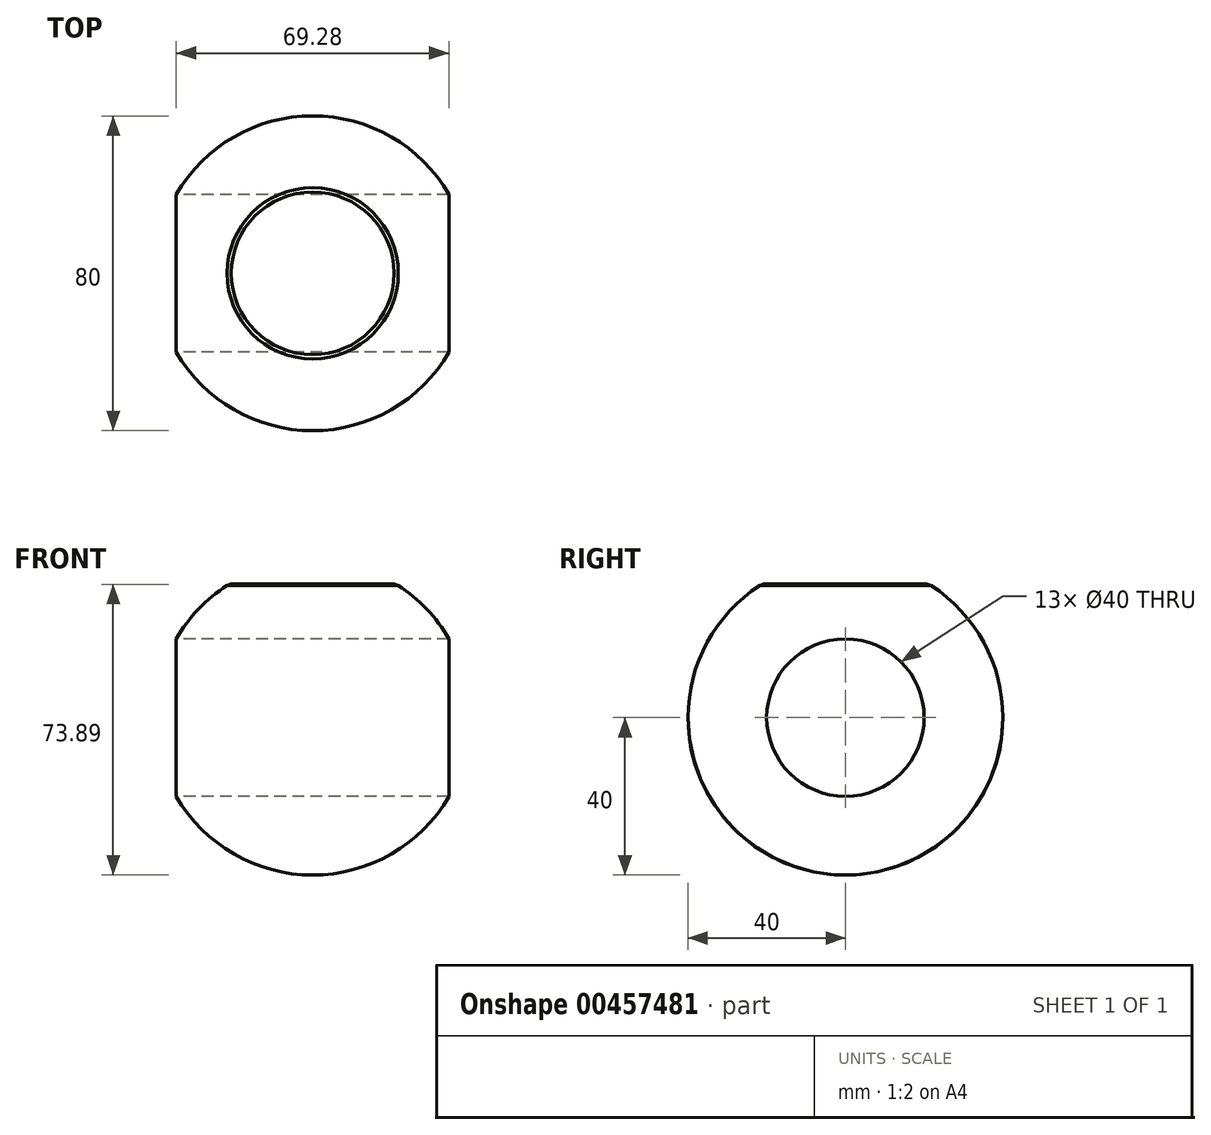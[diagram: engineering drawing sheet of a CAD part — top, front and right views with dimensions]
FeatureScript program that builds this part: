
annotation { "Feature Type Name" : "Feature", "Feature Type Description" : "" }
export const myFeature = defineFeature(function(context is Context, id is Id, definition is map)
    precondition{}
    {
        {
            var Q0;
            Q0=qCreatedBy(makeId("Top.planeOp"),FACE);
            var sketch = newSketch(context, id + "F0", { "sketchPlane" : qUnion([Q0])});
            skArc(sketch, "E0", {"start": v(0, -40) * mm, "mid": v(40, 0) * mm, "end": v(0, 40) * mm});
            skLineSegment(sketch, "E1", {"start": v(0, 40) * mm, "end": v(0, -40) * mm});
            skSolve(sketch);
        }
        {
            var Q0;
            Q0=makeQuery(id+"F0.imprint","IMPRINT",FACE,{"disambiguationData":[TD([[makeQuery(id+"F0.imprint","IMPRINT",EDGE,{"derivedFrom":sQuery(id+"F0.wireOp",EDGE,"E0")}),1.0]])]});
            var Q1;
            Q1=sQuery(id+"F0.wireOp",EDGE,"E1");
            revolve(context, id + "F1", {"entities" : qUnion([Q0]), "axis" : qUnion([Q1]), "revolveType" : RevolveType.FULL});
        }
        {
            var Q0;
            Q0=qCreatedBy(makeId("Right.planeOp"),FACE);
            var sketch = newSketch(context, id + "F2", { "sketchPlane" : qUnion([Q0])});
            skCircle(sketch, "E2", {"center": v(0, 0) * mm, "radius": 20 * mm});
            skSolve(sketch);
        }
        {
            var Q0;
            Q0 = qSketchRegion(id + "F2", true);
            extrude(context, id + "F3", {"entities" : qUnion([Q0]), "operationType" : NewBodyOperationType.REMOVE, "endBound" : BoundingType.SYMMETRIC, "depth" : 100 * mm});
        }
        {
            var Q0;
            Q0=qCreatedBy(makeId("Right.planeOp"),FACE);
            var sketch = newSketch(context, id + "F4", { "sketchPlane" : qUnion([Q0])});
            skLineSegment(sketch, "E3.bottom", {"start": v(31.95, 33.9) * mm, "end": v(-30.46, 33.9) * mm});
            skLineSegment(sketch, "E3.top", {"start": v(31.95, 72.96) * mm, "end": v(-30.46, 72.96) * mm});
            skLineSegment(sketch, "E3.left", {"start": v(31.95, 33.9) * mm, "end": v(31.95, 72.96) * mm});
            skLineSegment(sketch, "E3.right", {"start": v(-30.46, 33.9) * mm, "end": v(-30.46, 72.96) * mm});
            skSolve(sketch);
        }
        {
            var Q0;
            Q0 = qSketchRegion(id + "F4", true);
            extrude(context, id + "F5", {"entities" : qUnion([Q0]), "operationType" : NewBodyOperationType.REMOVE, "endBound" : BoundingType.SYMMETRIC, "oppositeDirection" : true, "depth" : 100 * mm});
        }
        {
            var Q0;
            Q0=makeQuery(id+"F5.boolean.opBoolean","COPY",FACE,{"derivedFrom":makeQuery(id+"F5.opExtrude","SWEPT_FACE",FACE,{"disambiguationData":[OSD([sQuery(id+"F4.wireOp",EDGE,"E3.bottom")])]})});
            chamfer(context, id + "F6", {"entities" : qUnion([Q0]), "width" : 2 * mm, "tangentPropagation" : true});
        }
    });
